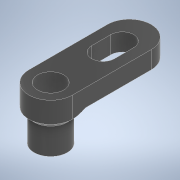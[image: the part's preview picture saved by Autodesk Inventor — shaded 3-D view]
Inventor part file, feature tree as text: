
AUTODESK INVENTOR PART (.ipt)
format: ipt  version: 2022.6 (Build 266554000, 554)  size: 284,160 bytes
history: native  units: mm
features: extrude x6, sketch x6, projected_geometry x5, chamfer x1
ambient origin geometry x8: Origin, YZ Plane, XZ Plane, XY Plane, X Axis, Y Axis, Z Axis, Center Point
bodies: Solid1 (feature_tree)
feature tree (18):
  extrude  "Extrusion1"  Depth=10.0mm
  extrude  "Extrusion2"  Depth=4.0mm TaperAngle=0.0deg
  extrude  "Extrusion4"  Depth=5.2mm
  extrude  "Extrusion5"  TaperAngle=0.0deg  [1 undecoded]
  extrude  "Extrusion6"  Depth=8.0mm
  extrude  "Extrusion7"  Depth=6.0mm
  chamfer  "Chamfer1"  Distance=5.0mm
  sketch  "Sketch1"  dims[d0=2.8mm d1=10.0mm]
  sketch  "Sketch2"  dims[d3=18.0mm d4=4.0mm d5=0.0mm]
  projected_geometry  "Projected Loop1"
  sketch  "Sketch4"  dims[d6=4.4mm d7=5.2mm]
  projected_geometry  "Projected Loop3"
  sketch  "Sketch5"  dims[d9=12.0mm d10=0.0mm d11=0.0mm]
  projected_geometry  "Projected Loop4"
  sketch  "Sketch6"  dims[d15=8.0mm d16=0.0mm d17=5.0mm]
  projected_geometry  "Projected Loop5"
  sketch  "Sketch7"  dims[d18=5.0mm d19=0.0mm d20=6.0mm d21=5.0mm d22=0.0mm d24=5.8mm d30=16.755161mm d31=0.45mm d32=260.0mm d34=360.0deg d36=2.0mm d37=0.0mm d39=7.6mm d40=2.0mm d41=2.0mm d42=45.0deg]
  projected_geometry  "Projected Loop6"
note: 1 required parameter value undecoded (feature->parameter linkage not recoverable at this tier; creation-order binding heuristic only, values carry confidence <= 0.55)
